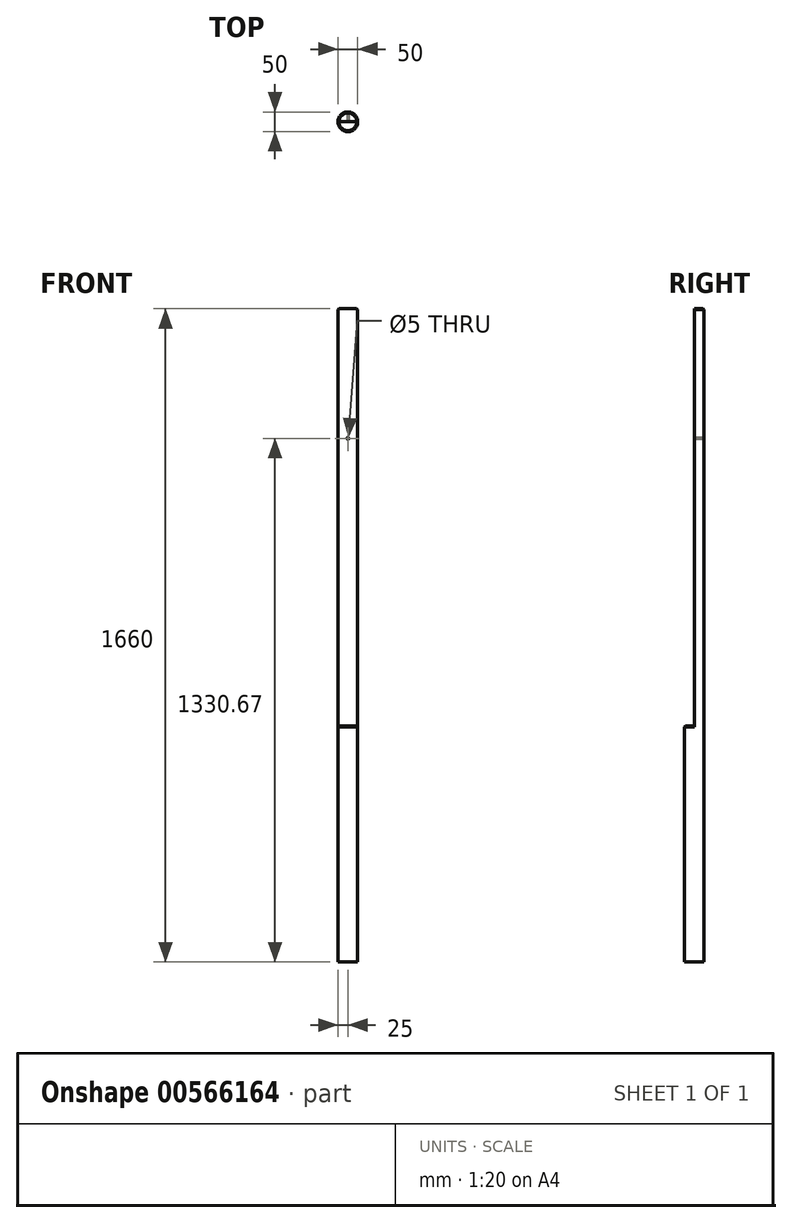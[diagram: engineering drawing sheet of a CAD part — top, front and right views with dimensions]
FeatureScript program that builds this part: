
annotation { "Feature Type Name" : "Feature", "Feature Type Description" : "" }
export const myFeature = defineFeature(function(context is Context, id is Id, definition is map)
    precondition{}
    {
        {
            var Q0;
            Q0=qCreatedBy(makeId("Top.planeOp"),FACE);
            var sketch = newSketch(context, id + "F0", { "sketchPlane" : qUnion([Q0])});
            skCircle(sketch, "E0", {"center": v(0, 0) * mm, "radius": 25 * mm});
            skLineSegment(sketch, "E1", {"start": v(-25, 0) * mm, "end": v(25, 0) * mm});
            skSolve(sketch);
        }
        {
            var Q0;
            {var subQ0=sQuery(id+"F0.wireOp",EDGE,"E1");Q0=makeQuery(id+"F0.imprint","IMPRINT",FACE,{"disambiguationData":[TD([[makeQuery(id+"F0.imprint","IMPRINT",EDGE,{"derivedFrom":subQ0}),1.0]])]});}
            extrude(context, id + "F1", {"entities" : qUnion([Q0]), "depth" : 1060 * mm, "offsetDistance" : 25.4 * mm});
        }
        {
            var Q0;
            {var subQ0=sQuery(id+"F0.wireOp",EDGE,"E1");Q0=makeQuery(id+"F0.imprint","IMPRINT",FACE,{"disambiguationData":[TD([[makeQuery(id+"F0.imprint","IMPRINT",EDGE,{"derivedFrom":subQ0}),-1.0]])]});}
            var Q1;
            {var subQ0=sQuery(id+"F0.wireOp",EDGE,"E1");Q1=makeQuery(id+"F0.imprint","IMPRINT",FACE,{"disambiguationData":[TD([[makeQuery(id+"F0.imprint","IMPRINT",EDGE,{"derivedFrom":subQ0}),1.0]])]});}
            extrude(context, id + "F2", {"entities" : qUnion([Q0, Q1]), "operationType" : NewBodyOperationType.ADD, "oppositeDirection" : true, "depth" : 600 * mm, "offsetDistance" : 25.4 * mm});
        }
        {
            var Q0;
            Q0=makeQuery(id+"F2.opExtrude","CAP_EDGE",EDGE,{"disambiguationData":[OSD([sQuery(id+"F0.wireOp",EDGE,"E0")])],"isStart":true});
            chamfer(context, id + "F3", {"entities" : qUnion([Q0]), "width" : 2.54 * mm, "tangentPropagation" : true});
        }
        {
            var Q0;
            Q0=makeQuery(id+"F1.opExtrude","CAP_EDGE",EDGE,{"disambiguationData":[OSD([sQuery(id+"F0.wireOp",EDGE,"E0")])],"isStart":false});
            chamfer(context, id + "F4", {"entities" : qUnion([Q0]), "width" : 2.54 * mm, "tangentPropagation" : true});
        }
        {
            var Q0;
            Q0=qCreatedBy(makeId("Front.planeOp"),FACE);
            var sketch = newSketch(context, id + "F5", { "sketchPlane" : qUnion([Q0])});
            skCircle(sketch, "E2", {"center": v(0, 730.67) * mm, "radius": 2.5 * mm});
            skLineSegment(sketch, "E3", {"start": v(0, 730.67) * mm, "end": v(0, 728.17) * mm});
            skSolve(sketch);
        }
        {
            var Q0;
            Q0=sQuery(id+"F5.wireOp",VERTEX,"E2.center");
            var Q1;
            Q1=makeQuery(id+"F1.opExtrude","SWEPT_BODY",BODY,{"disambiguationData":[OSD([sQuery(id+"F0.wireOp",EDGE,"E0"),sQuery(id+"F0.wireOp",EDGE,"E1")])]});
            hole(context, id + "F6", {"style" : HoleStyle.SIMPLE, "endStyle" : HoleEndStyle.THROUGH, "holeDiameter" : 5 * mm, "isTappedThrough" : true, "tappedDepth" : 12 * mm, "tapClearance" : 3, "locations" : qUnion([Q0]), "scope" : qUnion([Q1])});
        }
    });
